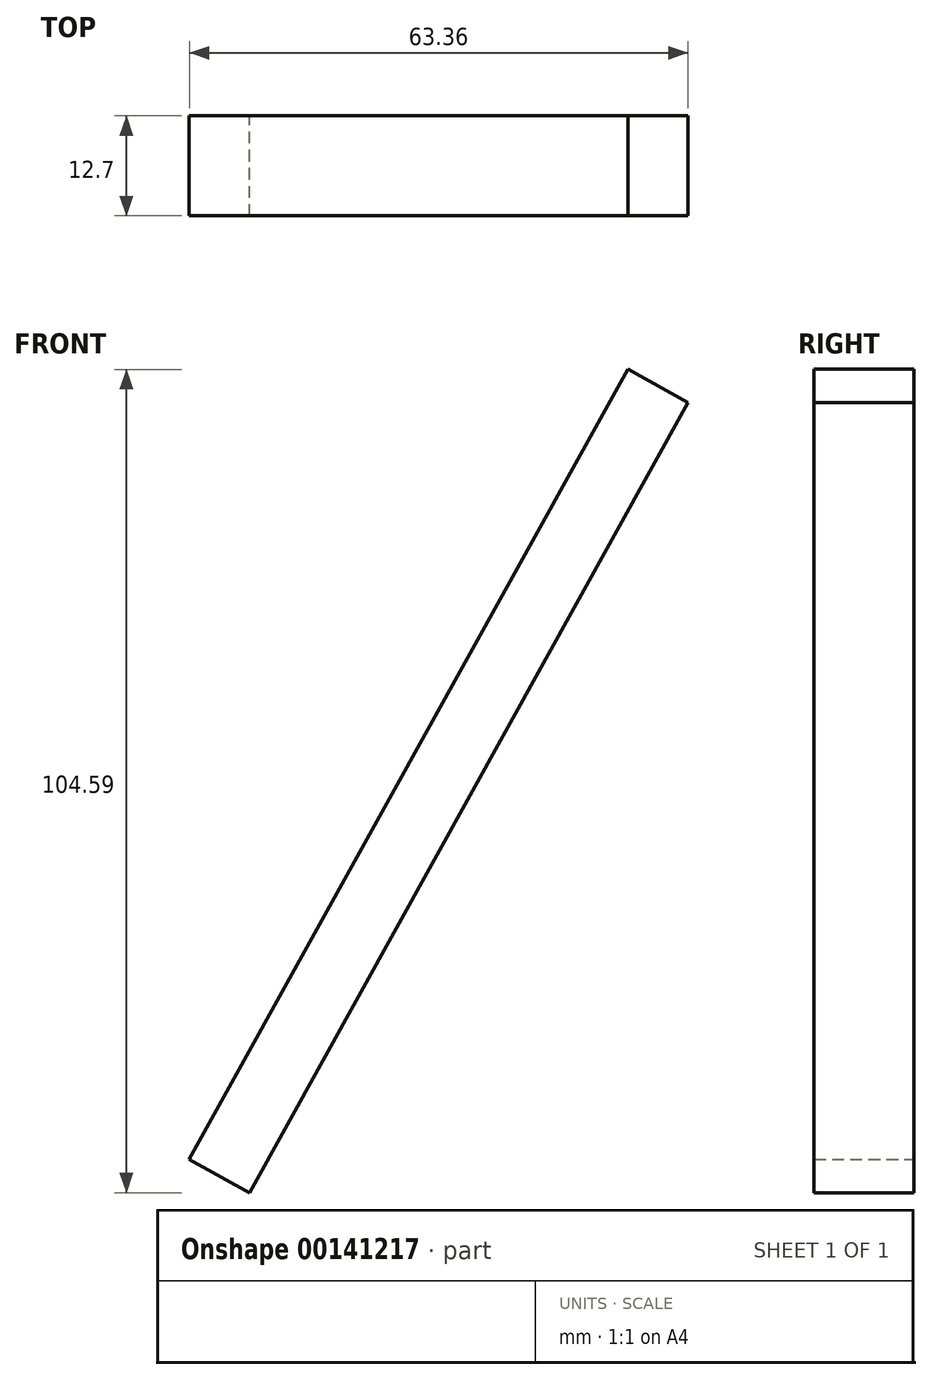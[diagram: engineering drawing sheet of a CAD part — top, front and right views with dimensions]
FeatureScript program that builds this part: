
annotation { "Feature Type Name" : "Feature", "Feature Type Description" : "" }
export const myFeature = defineFeature(function(context is Context, id is Id, definition is map)
    precondition{}
    {
        {
            var Q0;
            Q0=qCreatedBy(makeId("Front.planeOp"),FACE);
            var sketch = newSketch(context, id + "F0", { "sketchPlane" : qUnion([Q0])});
            skLineSegment(sketch, "E0", {"start": v(43.03, 36.64) * mm, "end": v(-12.68, -63.7) * mm});
            skLineSegment(sketch, "E1", {"start": v(-12.68, -63.7) * mm, "end": v(-20.33, -59.46) * mm});
            skLineSegment(sketch, "E2", {"start": v(-20.33, -59.46) * mm, "end": v(35.38, 40.9) * mm});
            skLineSegment(sketch, "E3", {"start": v(35.38, 40.9) * mm, "end": v(43.03, 36.64) * mm});
            skSolve(sketch);
        }
        {
            var Q0;
            Q0 = qSketchRegion(id + "F0", true);
            extrude(context, id + "F1", {"entities" : qUnion([Q0]), "depth" : 12.7 * mm});
        }
    });
